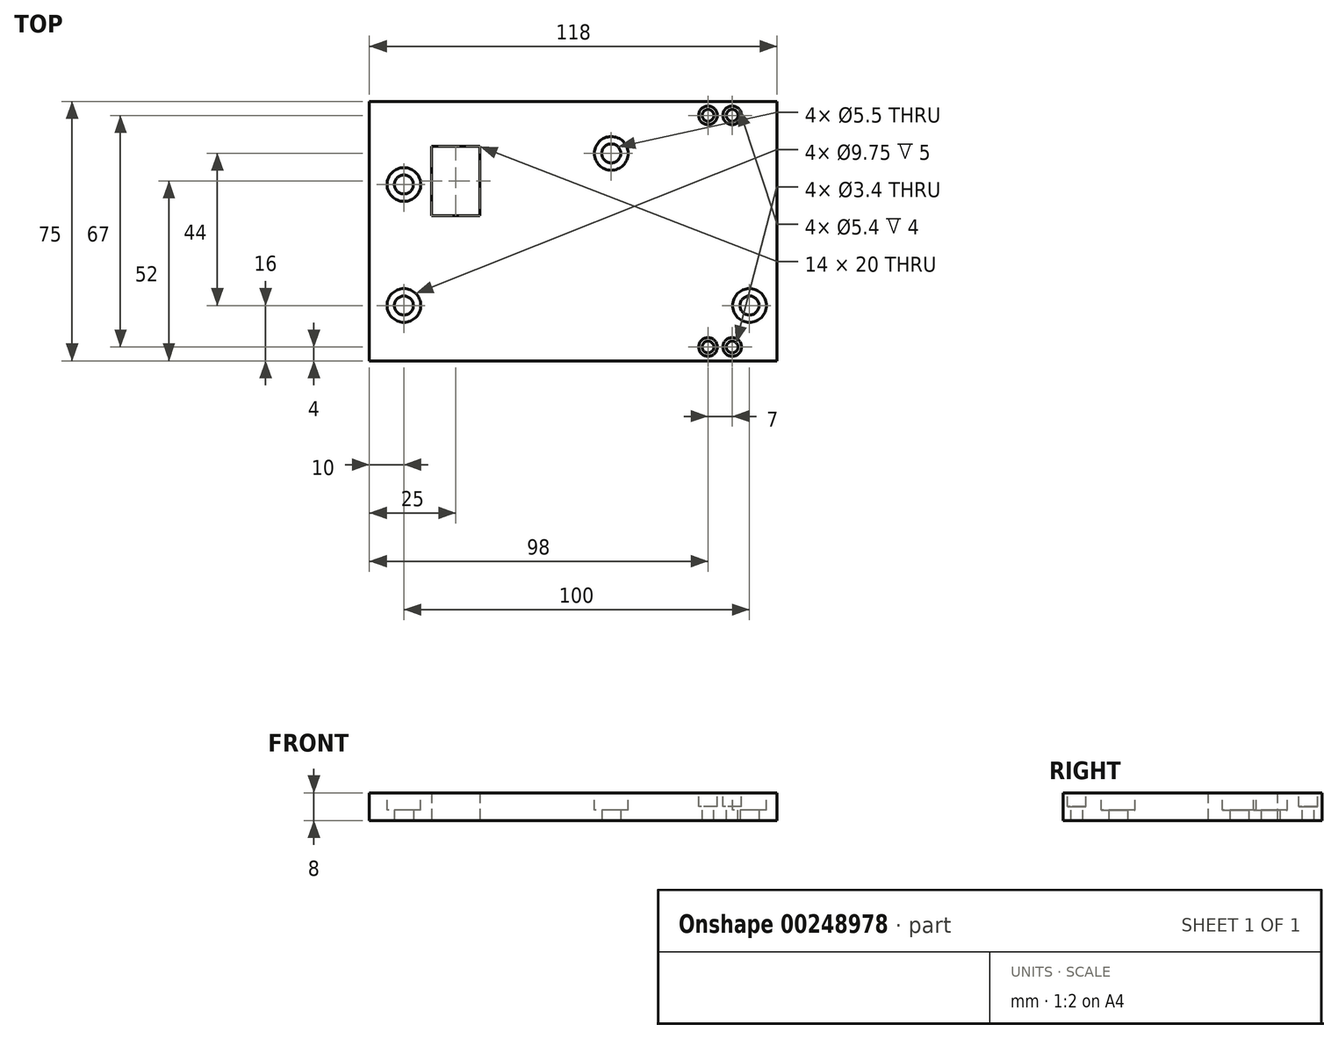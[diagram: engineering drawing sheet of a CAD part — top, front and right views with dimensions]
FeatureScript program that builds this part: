
annotation { "Feature Type Name" : "Feature", "Feature Type Description" : "" }
export const myFeature = defineFeature(function(context is Context, id is Id, definition is map)
    precondition{}
    {
        {
            var Q0;
            Q0=qCreatedBy(makeId("Top.planeOp"),FACE);
            var sketch = newSketch(context, id + "F0", { "sketchPlane" : qUnion([Q0])});
            skLineSegment(sketch, "E0.bottom", {"start": v(59, 37.5) * mm, "end": v(-59, 37.5) * mm});
            skLineSegment(sketch, "E0.top", {"start": v(59, -37.5) * mm, "end": v(-59, -37.5) * mm});
            skLineSegment(sketch, "E0.left", {"start": v(59, 37.5) * mm, "end": v(59, -37.5) * mm});
            skLineSegment(sketch, "E0.right", {"start": v(-59, 37.5) * mm, "end": v(-59, -37.5) * mm});
            skPoint(sketch, "E0.middle", {"position": v(0, 0) * mm});
            skCircle(sketch, "E1", {"center": v(-49, -21.5) * mm, "radius": 2.75 * mm});
            skCircle(sketch, "E2", {"center": v(51, -21.5) * mm, "radius": 2.75 * mm});
            skCircle(sketch, "E3", {"center": v(11, 22.5) * mm, "radius": 2.75 * mm});
            skCircle(sketch, "E4", {"center": v(-49, 13.5) * mm, "radius": 2.75 * mm});
            skLineSegment(sketch, "E5.bottom", {"start": v(-41, 24.5) * mm, "end": v(-27, 24.5) * mm});
            skLineSegment(sketch, "E5.top", {"start": v(-41, 4.5) * mm, "end": v(-27, 4.5) * mm});
            skLineSegment(sketch, "E5.left", {"start": v(-41, 24.5) * mm, "end": v(-41, 4.5) * mm});
            skLineSegment(sketch, "E5.right", {"start": v(-27, 24.5) * mm, "end": v(-27, 4.5) * mm});
            skCircle(sketch, "E6", {"center": v(39, -33.5) * mm, "radius": 1.6 * mm});
            skCircle(sketch, "E7", {"center": v(46, -33.5) * mm, "radius": 1.6 * mm});
            skCircle(sketch, "E8", {"center": v(39, 33.5) * mm, "radius": 1.6 * mm});
            skCircle(sketch, "E9", {"center": v(46, 33.5) * mm, "radius": 1.6 * mm});
            skSolve(sketch);
        }
        {
            var Q0;
            Q0=makeQuery(id+"F0.imprint","IMPRINT",FACE,{"disambiguationData":[TD([[makeQuery(id+"F0.imprint","IMPRINT",EDGE,{"derivedFrom":sQuery(id+"F0.wireOp",EDGE,"E0.bottom")}),1.0]])]});
            extrude(context, id + "F1", {"entities" : qUnion([Q0]), "depth" : 8 * mm});
        }
        {
            var Q0;
            Q0=makeQuery(id+"F1.opExtrude","CAP_FACE",FACE,{"disambiguationData":[OSD([sQuery(id+"F0.wireOp",EDGE,"E0.bottom"),sQuery(id+"F0.wireOp",EDGE,"E0.top"),sQuery(id+"F0.wireOp",EDGE,"E0.left"),sQuery(id+"F0.wireOp",EDGE,"E0.right"),sQuery(id+"F0.wireOp",EDGE,"E1"),sQuery(id+"F0.wireOp",EDGE,"E2"),sQuery(id+"F0.wireOp",EDGE,"E3"),sQuery(id+"F0.wireOp",EDGE,"E4"),sQuery(id+"F0.wireOp",EDGE,"E5.bottom"),sQuery(id+"F0.wireOp",EDGE,"E5.top"),sQuery(id+"F0.wireOp",EDGE,"E5.left"),sQuery(id+"F0.wireOp",EDGE,"E5.right"),sQuery(id+"F0.wireOp",EDGE,"E6"),sQuery(id+"F0.wireOp",EDGE,"E7"),sQuery(id+"F0.wireOp",EDGE,"E8"),sQuery(id+"F0.wireOp",EDGE,"E9")])],"isStart":false});
            var sketch = newSketch(context, id + "F2", { "sketchPlane" : qUnion([Q0])});
            skPoint(sketch, "E10", {"position": v(-49, 13.5) * mm});
            skPoint(sketch, "E11", {"position": v(11, 22.5) * mm});
            skPoint(sketch, "E12", {"position": v(39, 33.5) * mm});
            skPoint(sketch, "E13", {"position": v(46, 33.5) * mm});
            skPoint(sketch, "E14", {"position": v(51, -21.5) * mm});
            skPoint(sketch, "E15", {"position": v(46, -33.5) * mm});
            skPoint(sketch, "E16", {"position": v(39, -33.5) * mm});
            skPoint(sketch, "E17", {"position": v(-49, -21.5) * mm});
            skSolve(sketch);
        }
        {
            var Q0;
            Q0=sQuery(id+"F2.wireOp",VERTEX,"E10");
            var Q1;
            Q1=sQuery(id+"F2.wireOp",VERTEX,"E11");
            var Q2;
            Q2=sQuery(id+"F2.wireOp",VERTEX,"E14");
            var Q3;
            Q3=sQuery(id+"F2.wireOp",VERTEX,"E17");
            var Q4;
            Q4=makeQuery(id+"F1.opExtrude","SWEPT_BODY",BODY,{"disambiguationData":[OSD([sQuery(id+"F0.wireOp",EDGE,"E0.bottom"),sQuery(id+"F0.wireOp",EDGE,"E0.top"),sQuery(id+"F0.wireOp",EDGE,"E0.left"),sQuery(id+"F0.wireOp",EDGE,"E0.right"),sQuery(id+"F0.wireOp",EDGE,"E1"),sQuery(id+"F0.wireOp",EDGE,"E2"),sQuery(id+"F0.wireOp",EDGE,"E3"),sQuery(id+"F0.wireOp",EDGE,"E4"),sQuery(id+"F0.wireOp",EDGE,"E5.bottom"),sQuery(id+"F0.wireOp",EDGE,"E5.top"),sQuery(id+"F0.wireOp",EDGE,"E5.left"),sQuery(id+"F0.wireOp",EDGE,"E5.right"),sQuery(id+"F0.wireOp",EDGE,"E6"),sQuery(id+"F0.wireOp",EDGE,"E7"),sQuery(id+"F0.wireOp",EDGE,"E8"),sQuery(id+"F0.wireOp",EDGE,"E9")])]});
            hole(context, id + "F3", {"style" : HoleStyle.C_BORE, "endStyle" : HoleEndStyle.BLIND, "holeDiameter" : 5.5 * mm, "cBoreDiameter" : 9.75 * mm, "cBoreDepth" : 5 * mm, "holeDepth" : 8 * mm, "tappedDepth" : 12 * mm, "tapClearance" : 3, "startFromSketch" : true, "locations" : qUnion([Q0, Q1, Q2, Q3]), "scope" : qUnion([Q4])});
        }
        {
            var Q0;
            Q0=sQuery(id+"F2.wireOp",VERTEX,"E16");
            var Q1;
            Q1=sQuery(id+"F2.wireOp",VERTEX,"E15");
            var Q2;
            Q2=sQuery(id+"F2.wireOp",VERTEX,"E12");
            var Q3;
            Q3=sQuery(id+"F2.wireOp",VERTEX,"E13");
            var Q4;
            Q4=makeQuery(id+"F1.opExtrude","SWEPT_BODY",BODY,{"disambiguationData":[OSD([sQuery(id+"F0.wireOp",EDGE,"E0.bottom"),sQuery(id+"F0.wireOp",EDGE,"E0.top"),sQuery(id+"F0.wireOp",EDGE,"E0.left"),sQuery(id+"F0.wireOp",EDGE,"E0.right"),sQuery(id+"F0.wireOp",EDGE,"E1"),sQuery(id+"F0.wireOp",EDGE,"E2"),sQuery(id+"F0.wireOp",EDGE,"E3"),sQuery(id+"F0.wireOp",EDGE,"E4"),sQuery(id+"F0.wireOp",EDGE,"E5.bottom"),sQuery(id+"F0.wireOp",EDGE,"E5.top"),sQuery(id+"F0.wireOp",EDGE,"E5.left"),sQuery(id+"F0.wireOp",EDGE,"E5.right"),sQuery(id+"F0.wireOp",EDGE,"E6"),sQuery(id+"F0.wireOp",EDGE,"E7"),sQuery(id+"F0.wireOp",EDGE,"E8"),sQuery(id+"F0.wireOp",EDGE,"E9")])]});
            hole(context, id + "F4", {"style" : HoleStyle.C_BORE, "endStyle" : HoleEndStyle.BLIND, "holeDiameter" : 3.4 * mm, "cBoreDiameter" : 5.4 * mm, "cBoreDepth" : 4 * mm, "holeDepth" : 8 * mm, "tappedDepth" : 12 * mm, "tapClearance" : 3, "startFromSketch" : true, "locations" : qUnion([Q0, Q1, Q2, Q3]), "scope" : qUnion([Q4])});
        }
    });
